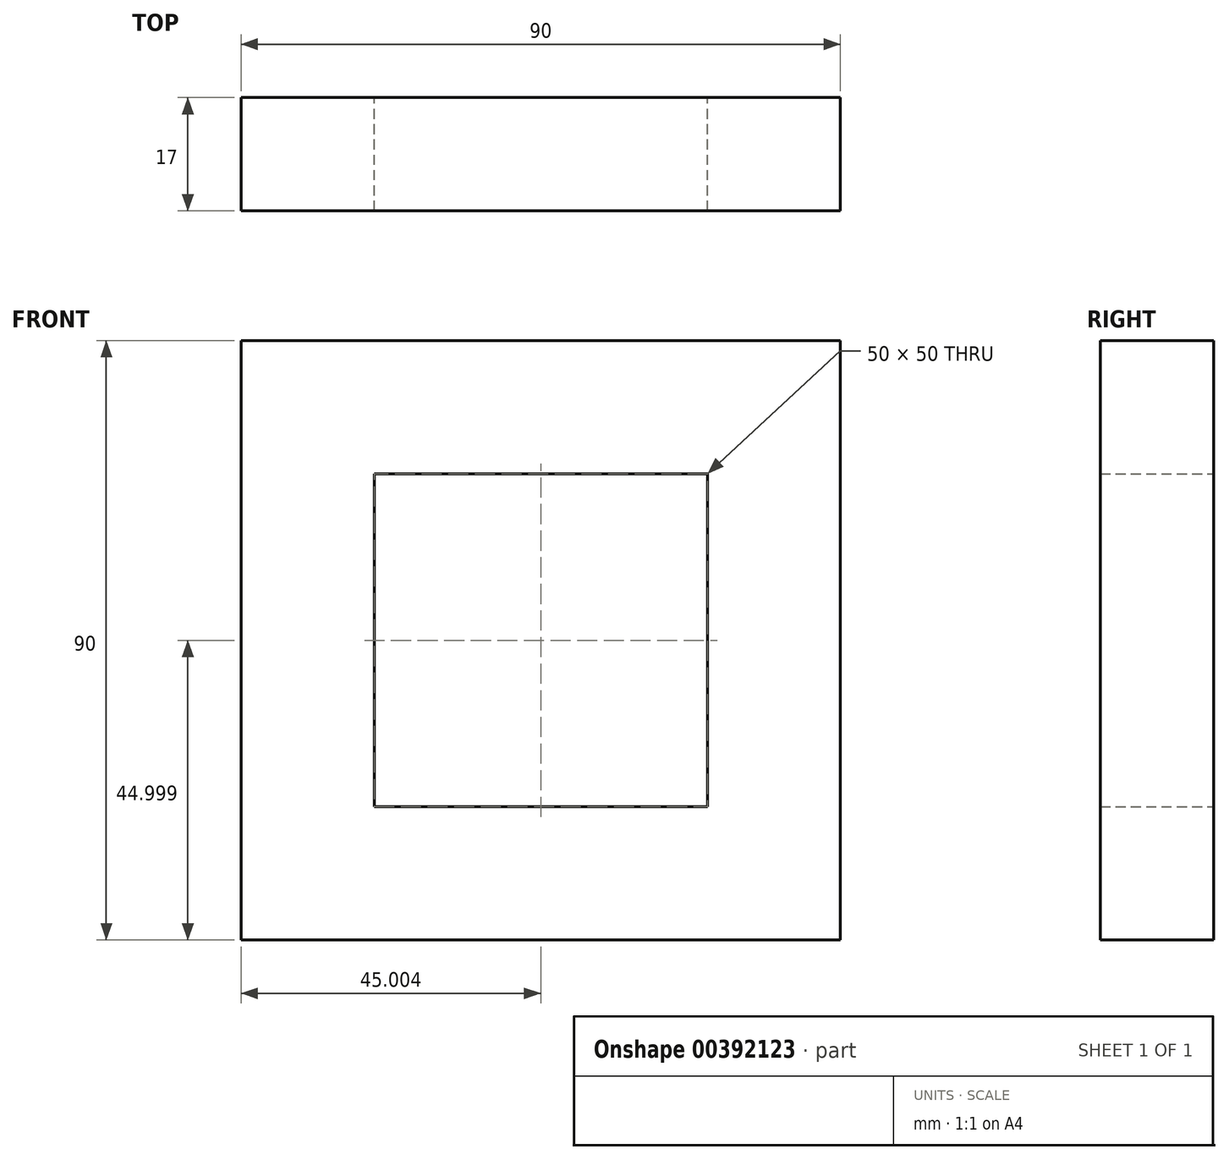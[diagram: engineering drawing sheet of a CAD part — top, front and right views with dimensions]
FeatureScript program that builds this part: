
annotation { "Feature Type Name" : "Feature", "Feature Type Description" : "" }
export const myFeature = defineFeature(function(context is Context, id is Id, definition is map)
    precondition{}
    {
        {
            var Q0;
            Q0=qCreatedBy(makeId("Front.planeOp"),FACE);
            var sketch = newSketch(context, id + "F0", { "sketchPlane" : qUnion([Q0])});
            skLineSegment(sketch, "E0.bottom", {"start": v(-47.1, 48.09) * mm, "end": v(42.9, 48.09) * mm});
            skLineSegment(sketch, "E0.top", {"start": v(-47.1, -41.91) * mm, "end": v(42.9, -41.91) * mm});
            skLineSegment(sketch, "E0.left", {"start": v(-47.1, 48.09) * mm, "end": v(-47.1, -41.91) * mm});
            skLineSegment(sketch, "E0.right", {"start": v(42.9, 48.09) * mm, "end": v(42.9, -41.91) * mm});
            skSolve(sketch);
        }
        {
            var Q0;
            Q0=makeQuery(id+"F0.imprint","IMPRINT",FACE,{"disambiguationData":[TD([[makeQuery(id+"F0.imprint","IMPRINT",EDGE,{"derivedFrom":sQuery(id+"F0.wireOp",EDGE,"E0.bottom")}),-1.0]])]});
            extrude(context, id + "F1", {"entities" : qUnion([Q0]), "depth" : 17 * mm});
        }
        {
            var Q0;
            Q0=makeQuery(id+"F1.opExtrude","CAP_FACE",FACE,{"disambiguationData":[OSD([sQuery(id+"F0.wireOp",EDGE,"E0.bottom"),sQuery(id+"F0.wireOp",EDGE,"E0.top"),sQuery(id+"F0.wireOp",EDGE,"E0.left"),sQuery(id+"F0.wireOp",EDGE,"E0.right")])],"isStart":true});
            var Q1;
            Q1=makeQuery(id+"F1.opExtrude","CAP_FACE",FACE,{"disambiguationData":[OSD([sQuery(id+"F0.wireOp",EDGE,"E0.bottom"),sQuery(id+"F0.wireOp",EDGE,"E0.top"),sQuery(id+"F0.wireOp",EDGE,"E0.left"),sQuery(id+"F0.wireOp",EDGE,"E0.right")])],"isStart":false});
            shell(context, id + "F2", {"entities" : qUnion([Q0, Q1]), "thickness" : 20 * mm});
        }
    });
